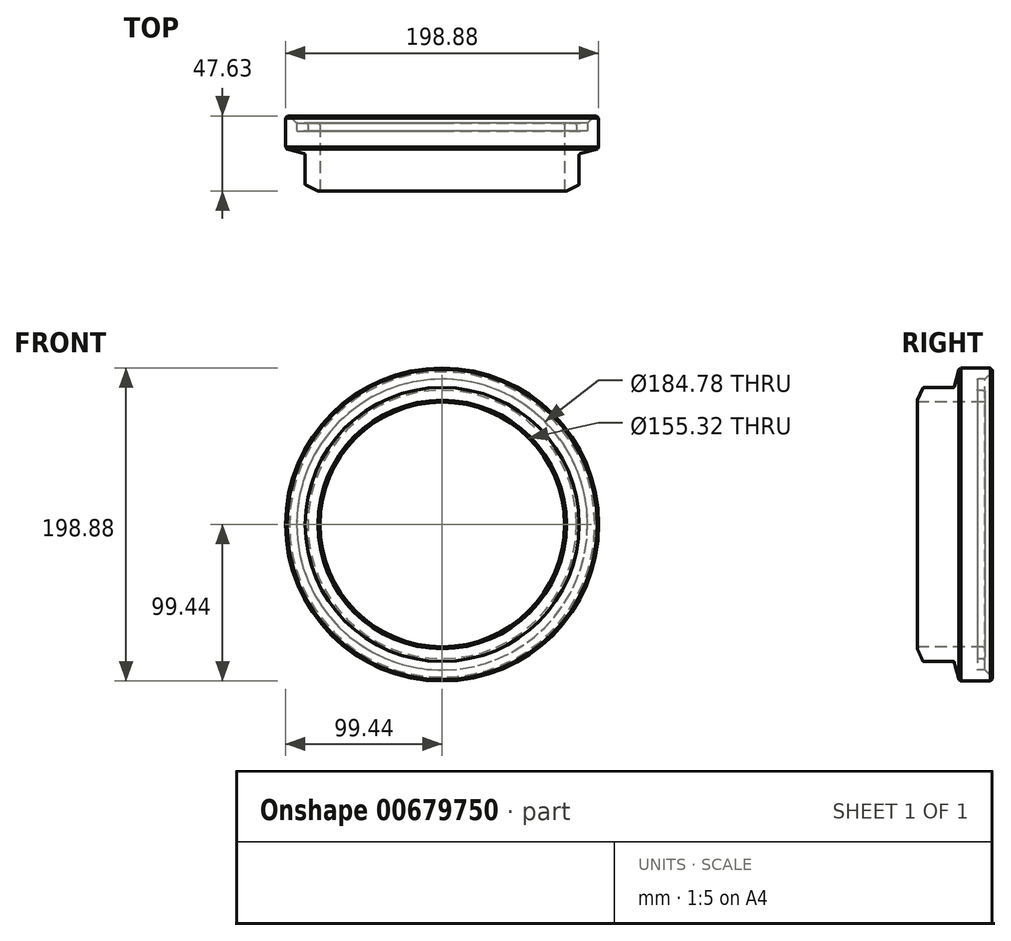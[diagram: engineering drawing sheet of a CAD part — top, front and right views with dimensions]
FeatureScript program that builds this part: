
annotation { "Feature Type Name" : "Feature", "Feature Type Description" : "" }
export const myFeature = defineFeature(function(context is Context, id is Id, definition is map)
    precondition{}
    {
        {
            var Q0;
            Q0=qCreatedBy(makeId("Right.planeOp"),FACE);
            var sketch = newSketch(context, id + "F0", { "sketchPlane" : qUnion([Q0])});
            skLineSegment(sketch, "E0", {"start": v(-20.83, 77.66) * mm, "end": v(20.83, 77.66) * mm});
            skPoint(sketch, "E1", {"position": v(0, 77.66) * mm});
            skLineSegment(sketch, "E2", {"start": v(20.83, 85.26) * mm, "end": v(17.27, 85.26) * mm});
            skLineSegment(sketch, "E3", {"start": v(16.57, 86.02) * mm, "end": v(16.57, 91.63) * mm});
            skLineSegment(sketch, "E4", {"start": v(21.53, 84.5) * mm, "end": v(21.53, 78.42) * mm});
            skLineSegment(sketch, "E5", {"start": v(1.84, 87) * mm, "end": v(5.18, 99.44) * mm});
            skLineSegment(sketch, "E6", {"start": v(-17.77, 87) * mm, "end": v(-21.53, 78.93) * mm});
            skLineSegment(sketch, "E7", {"start": v(21.53, 92.4) * mm, "end": v(26.1, 96.96) * mm});
            skLineSegment(sketch, "E8", {"start": v(26.1, 99.44) * mm, "end": v(26.1, 96.96) * mm});
            skLineSegment(sketch, "E9", {"start": v(21.53, 92.4) * mm, "end": v(17.34, 92.4) * mm});
            skLineSegment(sketch, "E10", {"start": v(-21.53, 78.74) * mm, "end": v(-21.53, 78.4) * mm});
            skLineSegment(sketch, "E11", {"start": v(-17.23, 87) * mm, "end": v(1.24, 87) * mm});
            skLineSegment(sketch, "E12", {"start": v(5.18, 99.44) * mm, "end": v(26.1, 99.44) * mm});
            skLineSegment(sketch, "E13", {"start": v(-49.6, 0) * mm, "end": v(55.99, 0) * mm, "construction": true});
            skPoint(sketch, "E14.visualSharp", {"position": v(-21.53, 78.93) * mm});
            skPoint(sketch, "E15.visualSharp", {"position": v(21.53, 85.26) * mm});
            skPoint(sketch, "E16.visualSharp", {"position": v(16.57, 85.26) * mm});
            skPoint(sketch, "E17.visualSharp", {"position": v(1.84, 87) * mm});
            skPoint(sketch, "E18.visualSharp", {"position": v(16.57, 92.4) * mm});
            skPoint(sketch, "E19.visualSharp", {"position": v(21.53, 77.66) * mm});
            skPoint(sketch, "E20.visualSharp", {"position": v(-21.53, 77.66) * mm});
            skPoint(sketch, "E21.visualSharp", {"position": v(-17.77, 87) * mm});
            skLineSegment(sketch, "E22", {"start": v(16.57, 92.4) * mm, "end": v(21.53, 92.4) * mm});
            skLineSegment(sketch, "E23", {"start": v(16.57, 92.4) * mm, "end": v(16.57, 85.26) * mm});
            skLineSegment(sketch, "E24", {"start": v(16.57, 85.26) * mm, "end": v(21.53, 85.26) * mm});
            skLineSegment(sketch, "E25", {"start": v(21.53, 85.26) * mm, "end": v(21.53, 77.66) * mm});
            skLineSegment(sketch, "E26", {"start": v(-21.53, 77.66) * mm, "end": v(21.53, 77.66) * mm});
            skLineSegment(sketch, "E27", {"start": v(-21.53, 77.66) * mm, "end": v(-21.53, 78.93) * mm});
            skLineSegment(sketch, "E28", {"start": v(1.84, 87) * mm, "end": v(-17.77, 87) * mm});
            skSolve(sketch);
        }
        {
            var Q0;
            {var subQ12=sQuery(id+"F0.wireOp",EDGE,"E5");Q0=makeQuery(id+"F0.imprint","IMPRINT",FACE,{"disambiguationData":[TD([[makeQuery(id+"F0.imprint","IMPRINT",EDGE,{"derivedFrom":subQ12}),-1.0]])]});}
            var Q1;
            Q1=sQuery(id+"F0.wireOp",EDGE,"E13");
            revolve(context, id + "F1", {"entities" : qUnion([Q0]), "axis" : qUnion([Q1]), "revolveType" : RevolveType.FULL});
        }
        {
            var Q0;
            Q0=makeQuery(id+"F1.opRevolve","SWEPT_EDGE",EDGE,{"disambiguationData":[OSD([sQuery(id+"F0.wireOp",EDGE,"E5"),sQuery(id+"F0.wireOp",EDGE,"E12")])]});
            var Q1;
            Q1=makeQuery(id+"F1.opRevolve","SWEPT_EDGE",EDGE,{"disambiguationData":[OSD([sQuery(id+"F0.wireOp",EDGE,"E8"),sQuery(id+"F0.wireOp",EDGE,"E12")])]});
            chamfer(context, id + "F2", {"entities" : qUnion([Q0, Q1]), "width" : 1.27 * mm, "tangentPropagation" : true});
        }
        {
            var Q0;
            Q0=makeQuery(id+"F1.opRevolve","SWEPT_EDGE",EDGE,{"disambiguationData":[OSD([sQuery(id+"F0.wireOp",EDGE,"E26"),sQuery(id+"F0.wireOp",EDGE,"E27")])]});
            var Q1;
            Q1=makeQuery(id+"F1.opRevolve","SWEPT_EDGE",EDGE,{"disambiguationData":[OSD([sQuery(id+"F0.wireOp",EDGE,"E25"),sQuery(id+"F0.wireOp",EDGE,"E26")])]});
            fillet(context, id + "F3", {"entities" : qUnion([Q0, Q1]), "radius" : 1.27 * mm, "tangentPropagation" : true, "allowEdgeOverflow" : false});
        }
        {
            var Q0;
            Q0=makeQuery(id+"F1.opRevolve","SWEPT_EDGE",EDGE,{"disambiguationData":[OSD([sQuery(id+"F0.wireOp",EDGE,"E5"),sQuery(id+"F0.wireOp",EDGE,"E28")])]});
            var Q1;
            Q1=makeQuery(id+"F1.opRevolve","SWEPT_EDGE",EDGE,{"disambiguationData":[OSD([sQuery(id+"F0.wireOp",EDGE,"E6"),sQuery(id+"F0.wireOp",EDGE,"E28")])]});
            fillet(context, id + "F4", {"entities" : qUnion([Q0, Q1]), "radius" : 0.76 * mm, "tangentPropagation" : true, "allowEdgeOverflow" : false});
        }
        {
            var Q0;
            Q0=makeQuery(id+"F1.opRevolve","SWEPT_EDGE",EDGE,{"disambiguationData":[OSD([sQuery(id+"F0.wireOp",EDGE,"E22"),sQuery(id+"F0.wireOp",EDGE,"E23")])]});
            var Q1;
            Q1=makeQuery(id+"F1.opRevolve","SWEPT_EDGE",EDGE,{"disambiguationData":[OSD([sQuery(id+"F0.wireOp",EDGE,"E23"),sQuery(id+"F0.wireOp",EDGE,"E24")])]});
            fillet(context, id + "F5", {"entities" : qUnion([Q0, Q1]), "radius" : 0.38 * mm, "tangentPropagation" : true, "allowEdgeOverflow" : false});
        }
        {
            var Q0;
            Q0=makeQuery(id+"F1.opRevolve","SWEPT_EDGE",EDGE,{"disambiguationData":[OSD([sQuery(id+"F0.wireOp",EDGE,"E24"),sQuery(id+"F0.wireOp",EDGE,"E25")])]});
            fillet(context, id + "F6", {"entities" : qUnion([Q0]), "radius" : 1.27 * mm, "tangentPropagation" : true, "allowEdgeOverflow" : false});
        }
    });
